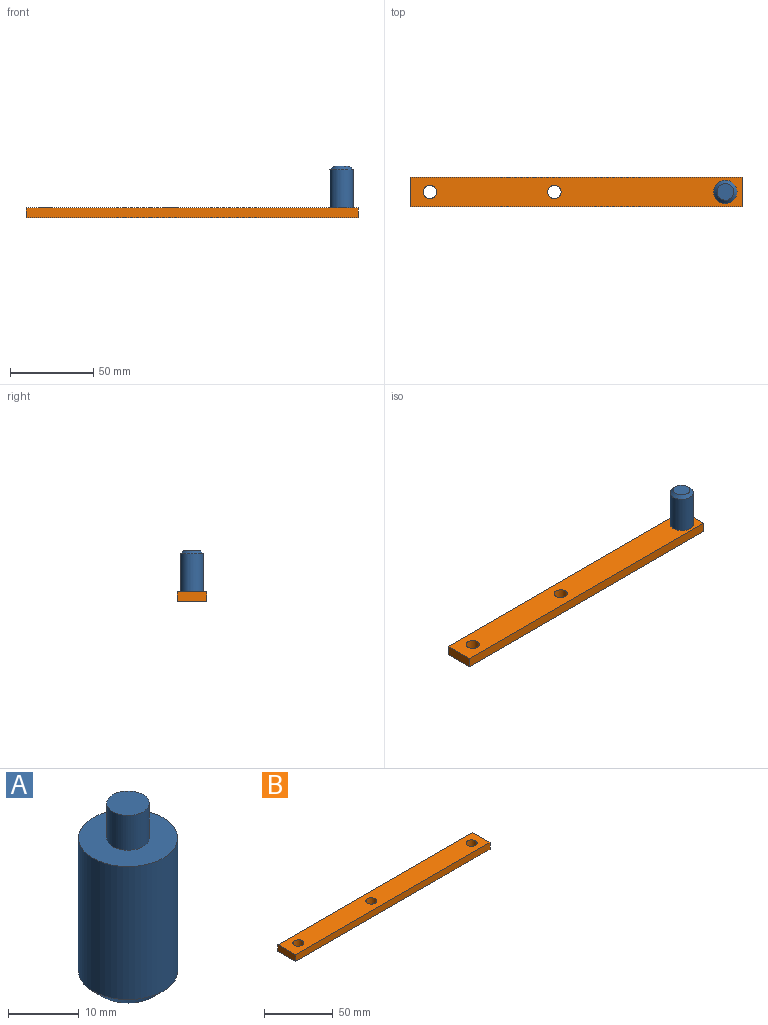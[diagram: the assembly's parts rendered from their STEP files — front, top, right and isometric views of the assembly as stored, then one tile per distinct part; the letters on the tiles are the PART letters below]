
ASSEMBLY  parts=2 mates=1
PART A: 6 faces, bbox 14x14x31 mm
  f0: cylinder r=3mm len=6mm, axis (0,0,-1), area 113.1mm2, adj f1,f4
  f1: plane 6x6mm, normal (0,0,1), area 28.3mm2, adj f0
  f2: cylinder r=7mm len=23mm, axis (0,0,1), area 1011.6mm2, adj f4,f5
  f3: plane 10x10mm, normal (0,0,-1), area 78.5mm2, adj f5
  f4: plane 14x14mm, normal (0,0,1), area 125.7mm2, adj f0,f2
  f5: cone r=7mm half-angle=45deg, axis (0,0,1), area 106.6mm2, adj f2,f3
PART B: 9 faces, bbox 200x18x6 mm
  f0: plane 18x6mm, normal (-1,0,0), area 108mm2, adj f1,f5,f7,f8
  f1: plane 200x6mm, normal (0,-1,0), area 1200mm2, adj f0,f2,f7,f8
  f2: plane 18x6mm, normal (1,0,0), area 108mm2, adj f1,f5,f7,f8
  f3: cylinder r=4mm len=8mm, axis (0,0,-1), area 150.8mm2, adj f7,f8
  f4: cylinder r=4mm len=8mm, axis (0,0,-1), area 150.8mm2, adj f7,f8
  f5: plane 200x6mm, normal (0,1,0), area 1200mm2, adj f0,f2,f7,f8
  f6: cylinder r=4mm len=8mm, axis (0,0,-1), area 150.8mm2, adj f7,f8
  f7: plane 200x18mm, normal (0,0,1), area 3449.2mm2, adj f0,f1,f2,f3,f4,f5,f6
  f8: plane 200x18mm, normal (0,0,-1), area 3449.2mm2, adj f0,f1,f2,f3,f4,f5,f6
PLACE A rot(axis=(1,0,0),180deg) t=(217.06,9.2,-7.64)mm
PLACE B t=(27.06,0.2,-13.64)mm
MATE fastened A.f2 <-> B.f6  axis (0,0,-1) through (217.06,9.2,-7.64)mm
